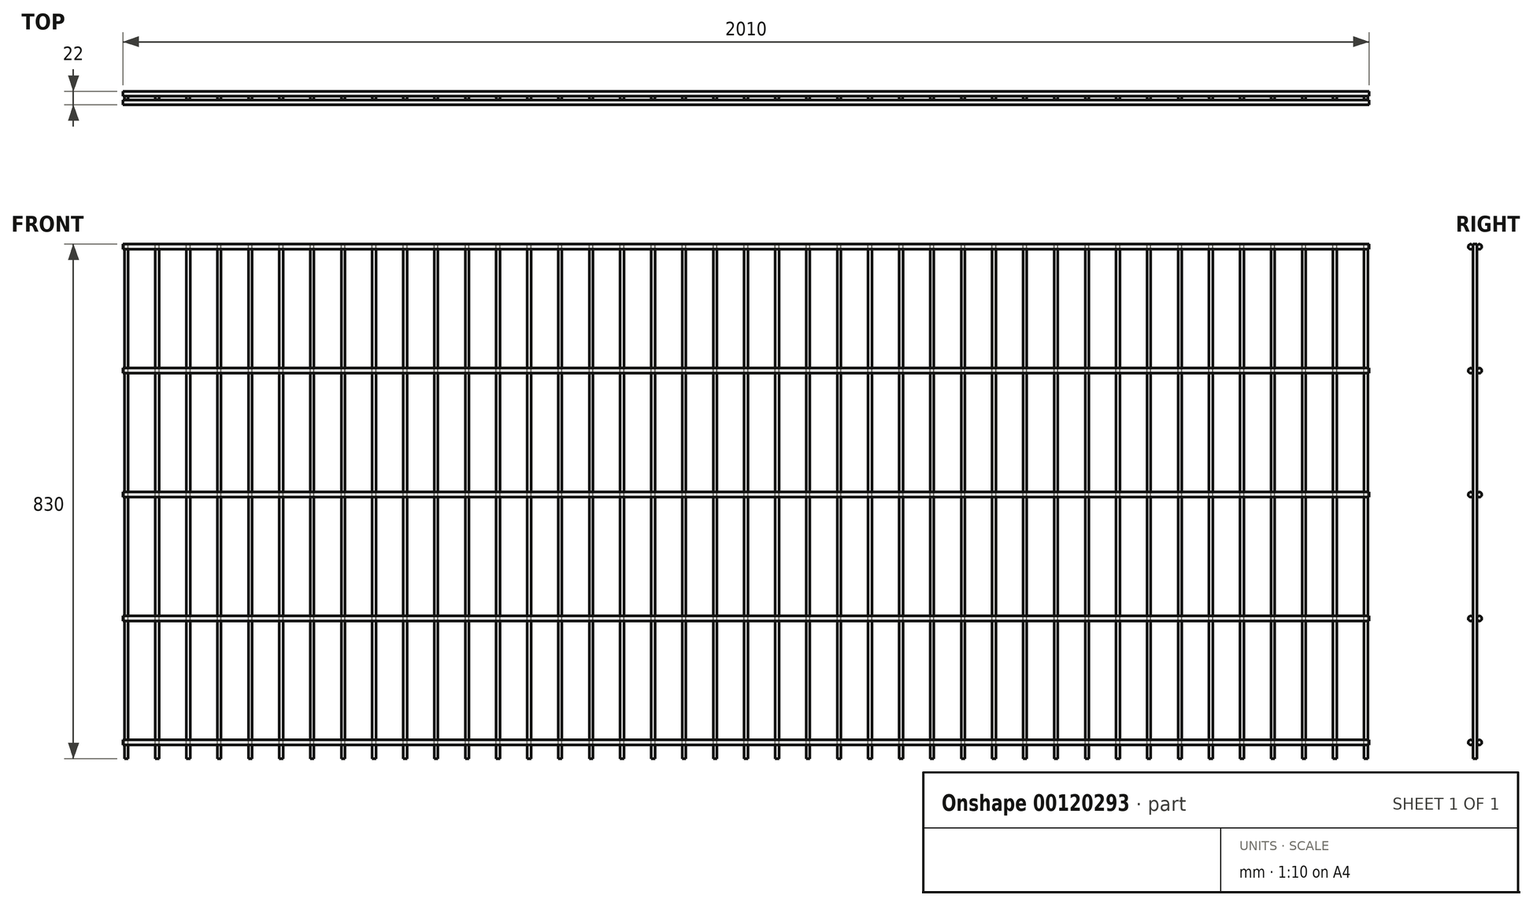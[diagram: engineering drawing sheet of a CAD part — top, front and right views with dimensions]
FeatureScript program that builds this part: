
annotation { "Feature Type Name" : "Feature", "Feature Type Description" : "" }
export const myFeature = defineFeature(function(context is Context, id is Id, definition is map)
    precondition{}
    {
        {
            var Q0;
            Q0=qCreatedBy(makeId("Top.planeOp"),FACE);
            var sketch = newSketch(context, id + "F0", { "sketchPlane" : qUnion([Q0])});
            skCircle(sketch, "E0", {"center": v(-100, 0) * mm, "radius": 3 * mm});
            skCircle(sketch, "E1", {"center": v(-150, 0) * mm, "radius": 3 * mm});
            skCircle(sketch, "E2", {"center": v(-50, 0) * mm, "radius": 3 * mm});
            skCircle(sketch, "E3", {"center": v(0, 0) * mm, "radius": 3 * mm});
            skCircle(sketch, "E4", {"center": v(100, 0) * mm, "radius": 3 * mm});
            skCircle(sketch, "E5", {"center": v(50, 0) * mm, "radius": 3 * mm});
            skCircle(sketch, "E6", {"center": v(150, 0) * mm, "radius": 3 * mm});
            skCircle(sketch, "E7", {"center": v(-450, 0) * mm, "radius": 3 * mm});
            skCircle(sketch, "E8", {"center": v(-500, 0) * mm, "radius": 3 * mm});
            skCircle(sketch, "E9", {"center": v(-400, 0) * mm, "radius": 3 * mm});
            skCircle(sketch, "E10", {"center": v(-350, 0) * mm, "radius": 3 * mm});
            skCircle(sketch, "E11", {"center": v(-250, 0) * mm, "radius": 3 * mm});
            skCircle(sketch, "E12", {"center": v(-300, 0) * mm, "radius": 3 * mm});
            skCircle(sketch, "E13", {"center": v(-200, 0) * mm, "radius": 3 * mm});
            skCircle(sketch, "E14", {"center": v(250, 0) * mm, "radius": 3 * mm});
            skCircle(sketch, "E15", {"center": v(200, 0) * mm, "radius": 3 * mm});
            skCircle(sketch, "E16", {"center": v(300, 0) * mm, "radius": 3 * mm});
            skCircle(sketch, "E17", {"center": v(350, 0) * mm, "radius": 3 * mm});
            skCircle(sketch, "E18", {"center": v(450, 0) * mm, "radius": 3 * mm});
            skCircle(sketch, "E19", {"center": v(400, 0) * mm, "radius": 3 * mm});
            skCircle(sketch, "E20", {"center": v(500, 0) * mm, "radius": 3 * mm});
            skCircle(sketch, "E21", {"center": v(600, 0) * mm, "radius": 3 * mm});
            skCircle(sketch, "E22", {"center": v(550, 0) * mm, "radius": 3 * mm});
            skCircle(sketch, "E23", {"center": v(650, 0) * mm, "radius": 3 * mm});
            skCircle(sketch, "E24", {"center": v(750, 0) * mm, "radius": 3 * mm});
            skCircle(sketch, "E25", {"center": v(700, 0) * mm, "radius": 3 * mm});
            skCircle(sketch, "E26", {"center": v(800, 0) * mm, "radius": 3 * mm});
            skCircle(sketch, "E27", {"center": v(850, 0) * mm, "radius": 3 * mm});
            skCircle(sketch, "E28", {"center": v(950, 0) * mm, "radius": 3 * mm});
            skCircle(sketch, "E29", {"center": v(900, 0) * mm, "radius": 3 * mm});
            skCircle(sketch, "E30", {"center": v(1000, 0) * mm, "radius": 3 * mm});
            skCircle(sketch, "E31", {"center": v(-950, 0) * mm, "radius": 3 * mm});
            skCircle(sketch, "E32", {"center": v(-1000, 0) * mm, "radius": 3 * mm});
            skCircle(sketch, "E33", {"center": v(-900, 0) * mm, "radius": 3 * mm});
            skCircle(sketch, "E34", {"center": v(-800, 0) * mm, "radius": 3 * mm});
            skCircle(sketch, "E35", {"center": v(-850, 0) * mm, "radius": 3 * mm});
            skCircle(sketch, "E36", {"center": v(-750, 0) * mm, "radius": 3 * mm});
            skCircle(sketch, "E37", {"center": v(-700, 0) * mm, "radius": 3 * mm});
            skCircle(sketch, "E38", {"center": v(-600, 0) * mm, "radius": 3 * mm});
            skCircle(sketch, "E39", {"center": v(-650, 0) * mm, "radius": 3 * mm});
            skCircle(sketch, "E40", {"center": v(-550, 0) * mm, "radius": 3 * mm});
            skSolve(sketch);
        }
        {
            var Q0;
            Q0=makeQuery(id+"F0.imprint","IMPRINT",FACE,{"disambiguationData":[TD([[makeQuery(id+"F0.imprint","IMPRINT",EDGE,{"derivedFrom":sQuery(id+"F0.wireOp",EDGE,"E24")}),1.0]])]});
            var Q1;
            Q1=makeQuery(id+"F0.imprint","IMPRINT",FACE,{"disambiguationData":[TD([[makeQuery(id+"F0.imprint","IMPRINT",EDGE,{"derivedFrom":sQuery(id+"F0.wireOp",EDGE,"E40")}),1.0]])]});
            var Q2;
            Q2=makeQuery(id+"F0.imprint","IMPRINT",FACE,{"disambiguationData":[TD([[makeQuery(id+"F0.imprint","IMPRINT",EDGE,{"derivedFrom":sQuery(id+"F0.wireOp",EDGE,"E28")}),1.0]])]});
            var Q3;
            Q3=makeQuery(id+"F0.imprint","IMPRINT",FACE,{"disambiguationData":[TD([[makeQuery(id+"F0.imprint","IMPRINT",EDGE,{"derivedFrom":sQuery(id+"F0.wireOp",EDGE,"E18")}),1.0]])]});
            var Q4;
            Q4=makeQuery(id+"F0.imprint","IMPRINT",FACE,{"disambiguationData":[TD([[makeQuery(id+"F0.imprint","IMPRINT",EDGE,{"derivedFrom":sQuery(id+"F0.wireOp",EDGE,"E34")}),1.0]])]});
            var Q5;
            Q5=makeQuery(id+"F0.imprint","IMPRINT",FACE,{"disambiguationData":[TD([[makeQuery(id+"F0.imprint","IMPRINT",EDGE,{"derivedFrom":sQuery(id+"F0.wireOp",EDGE,"E33")}),1.0]])]});
            var Q6;
            Q6=makeQuery(id+"F0.imprint","IMPRINT",FACE,{"disambiguationData":[TD([[makeQuery(id+"F0.imprint","IMPRINT",EDGE,{"derivedFrom":sQuery(id+"F0.wireOp",EDGE,"E17")}),1.0]])]});
            var Q7;
            Q7=makeQuery(id+"F0.imprint","IMPRINT",FACE,{"disambiguationData":[TD([[makeQuery(id+"F0.imprint","IMPRINT",EDGE,{"derivedFrom":sQuery(id+"F0.wireOp",EDGE,"E37")}),1.0]])]});
            var Q8;
            Q8=makeQuery(id+"F0.imprint","IMPRINT",FACE,{"disambiguationData":[TD([[makeQuery(id+"F0.imprint","IMPRINT",EDGE,{"derivedFrom":sQuery(id+"F0.wireOp",EDGE,"E30")}),1.0]])]});
            var Q9;
            Q9=makeQuery(id+"F0.imprint","IMPRINT",FACE,{"disambiguationData":[TD([[makeQuery(id+"F0.imprint","IMPRINT",EDGE,{"derivedFrom":sQuery(id+"F0.wireOp",EDGE,"E21")}),1.0]])]});
            var Q10;
            Q10=makeQuery(id+"F0.imprint","IMPRINT",FACE,{"disambiguationData":[TD([[makeQuery(id+"F0.imprint","IMPRINT",EDGE,{"derivedFrom":sQuery(id+"F0.wireOp",EDGE,"E25")}),1.0]])]});
            var Q11;
            Q11=makeQuery(id+"F0.imprint","IMPRINT",FACE,{"disambiguationData":[TD([[makeQuery(id+"F0.imprint","IMPRINT",EDGE,{"derivedFrom":sQuery(id+"F0.wireOp",EDGE,"E23")}),1.0]])]});
            var Q12;
            Q12=makeQuery(id+"F0.imprint","IMPRINT",FACE,{"disambiguationData":[TD([[makeQuery(id+"F0.imprint","IMPRINT",EDGE,{"derivedFrom":sQuery(id+"F0.wireOp",EDGE,"E39")}),1.0]])]});
            var Q13;
            Q13=makeQuery(id+"F0.imprint","IMPRINT",FACE,{"disambiguationData":[TD([[makeQuery(id+"F0.imprint","IMPRINT",EDGE,{"derivedFrom":sQuery(id+"F0.wireOp",EDGE,"E27")}),1.0]])]});
            var Q14;
            Q14=makeQuery(id+"F0.imprint","IMPRINT",FACE,{"disambiguationData":[TD([[makeQuery(id+"F0.imprint","IMPRINT",EDGE,{"derivedFrom":sQuery(id+"F0.wireOp",EDGE,"E12")}),1.0]])]});
            var Q15;
            Q15=makeQuery(id+"F0.imprint","IMPRINT",FACE,{"disambiguationData":[TD([[makeQuery(id+"F0.imprint","IMPRINT",EDGE,{"derivedFrom":sQuery(id+"F0.wireOp",EDGE,"E11")}),1.0]])]});
            var Q16;
            Q16=makeQuery(id+"F0.imprint","IMPRINT",FACE,{"disambiguationData":[TD([[makeQuery(id+"F0.imprint","IMPRINT",EDGE,{"derivedFrom":sQuery(id+"F0.wireOp",EDGE,"E10")}),1.0]])]});
            var Q17;
            Q17=makeQuery(id+"F0.imprint","IMPRINT",FACE,{"disambiguationData":[TD([[makeQuery(id+"F0.imprint","IMPRINT",EDGE,{"derivedFrom":sQuery(id+"F0.wireOp",EDGE,"E9")}),1.0]])]});
            var Q18;
            Q18=makeQuery(id+"F0.imprint","IMPRINT",FACE,{"disambiguationData":[TD([[makeQuery(id+"F0.imprint","IMPRINT",EDGE,{"derivedFrom":sQuery(id+"F0.wireOp",EDGE,"E8")}),1.0]])]});
            var Q19;
            Q19=makeQuery(id+"F0.imprint","IMPRINT",FACE,{"disambiguationData":[TD([[makeQuery(id+"F0.imprint","IMPRINT",EDGE,{"derivedFrom":sQuery(id+"F0.wireOp",EDGE,"E31")}),1.0]])]});
            var Q20;
            Q20=makeQuery(id+"F0.imprint","IMPRINT",FACE,{"disambiguationData":[TD([[makeQuery(id+"F0.imprint","IMPRINT",EDGE,{"derivedFrom":sQuery(id+"F0.wireOp",EDGE,"E7")}),1.0]])]});
            var Q21;
            Q21=makeQuery(id+"F0.imprint","IMPRINT",FACE,{"disambiguationData":[TD([[makeQuery(id+"F0.imprint","IMPRINT",EDGE,{"derivedFrom":sQuery(id+"F0.wireOp",EDGE,"E6")}),1.0]])]});
            var Q22;
            Q22=makeQuery(id+"F0.imprint","IMPRINT",FACE,{"disambiguationData":[TD([[makeQuery(id+"F0.imprint","IMPRINT",EDGE,{"derivedFrom":sQuery(id+"F0.wireOp",EDGE,"E5")}),1.0]])]});
            var Q23;
            Q23=makeQuery(id+"F0.imprint","IMPRINT",FACE,{"disambiguationData":[TD([[makeQuery(id+"F0.imprint","IMPRINT",EDGE,{"derivedFrom":sQuery(id+"F0.wireOp",EDGE,"E4")}),1.0]])]});
            var Q24;
            Q24=makeQuery(id+"F0.imprint","IMPRINT",FACE,{"disambiguationData":[TD([[makeQuery(id+"F0.imprint","IMPRINT",EDGE,{"derivedFrom":sQuery(id+"F0.wireOp",EDGE,"E3")}),1.0]])]});
            var Q25;
            Q25=makeQuery(id+"F0.imprint","IMPRINT",FACE,{"disambiguationData":[TD([[makeQuery(id+"F0.imprint","IMPRINT",EDGE,{"derivedFrom":sQuery(id+"F0.wireOp",EDGE,"E2")}),1.0]])]});
            var Q26;
            Q26=makeQuery(id+"F0.imprint","IMPRINT",FACE,{"disambiguationData":[TD([[makeQuery(id+"F0.imprint","IMPRINT",EDGE,{"derivedFrom":sQuery(id+"F0.wireOp",EDGE,"E1")}),1.0]])]});
            var Q27;
            Q27=makeQuery(id+"F0.imprint","IMPRINT",FACE,{"disambiguationData":[TD([[makeQuery(id+"F0.imprint","IMPRINT",EDGE,{"derivedFrom":sQuery(id+"F0.wireOp",EDGE,"E0")}),1.0]])]});
            var Q28;
            Q28=makeQuery(id+"F0.imprint","IMPRINT",FACE,{"disambiguationData":[TD([[makeQuery(id+"F0.imprint","IMPRINT",EDGE,{"derivedFrom":sQuery(id+"F0.wireOp",EDGE,"E32")}),1.0]])]});
            var Q29;
            Q29=makeQuery(id+"F0.imprint","IMPRINT",FACE,{"disambiguationData":[TD([[makeQuery(id+"F0.imprint","IMPRINT",EDGE,{"derivedFrom":sQuery(id+"F0.wireOp",EDGE,"E16")}),1.0]])]});
            var Q30;
            Q30=makeQuery(id+"F0.imprint","IMPRINT",FACE,{"disambiguationData":[TD([[makeQuery(id+"F0.imprint","IMPRINT",EDGE,{"derivedFrom":sQuery(id+"F0.wireOp",EDGE,"E14")}),1.0]])]});
            var Q31;
            Q31=makeQuery(id+"F0.imprint","IMPRINT",FACE,{"disambiguationData":[TD([[makeQuery(id+"F0.imprint","IMPRINT",EDGE,{"derivedFrom":sQuery(id+"F0.wireOp",EDGE,"E13")}),1.0]])]});
            var Q32;
            Q32=makeQuery(id+"F0.imprint","IMPRINT",FACE,{"disambiguationData":[TD([[makeQuery(id+"F0.imprint","IMPRINT",EDGE,{"derivedFrom":sQuery(id+"F0.wireOp",EDGE,"E29")}),1.0]])]});
            var Q33;
            Q33=makeQuery(id+"F0.imprint","IMPRINT",FACE,{"disambiguationData":[TD([[makeQuery(id+"F0.imprint","IMPRINT",EDGE,{"derivedFrom":sQuery(id+"F0.wireOp",EDGE,"E36")}),1.0]])]});
            var Q34;
            Q34=makeQuery(id+"F0.imprint","IMPRINT",FACE,{"disambiguationData":[TD([[makeQuery(id+"F0.imprint","IMPRINT",EDGE,{"derivedFrom":sQuery(id+"F0.wireOp",EDGE,"E15")}),1.0]])]});
            var Q35;
            Q35=makeQuery(id+"F0.imprint","IMPRINT",FACE,{"disambiguationData":[TD([[makeQuery(id+"F0.imprint","IMPRINT",EDGE,{"derivedFrom":sQuery(id+"F0.wireOp",EDGE,"E20")}),1.0]])]});
            var Q36;
            Q36=makeQuery(id+"F0.imprint","IMPRINT",FACE,{"disambiguationData":[TD([[makeQuery(id+"F0.imprint","IMPRINT",EDGE,{"derivedFrom":sQuery(id+"F0.wireOp",EDGE,"E22")}),1.0]])]});
            var Q37;
            Q37=makeQuery(id+"F0.imprint","IMPRINT",FACE,{"disambiguationData":[TD([[makeQuery(id+"F0.imprint","IMPRINT",EDGE,{"derivedFrom":sQuery(id+"F0.wireOp",EDGE,"E38")}),1.0]])]});
            var Q38;
            Q38=makeQuery(id+"F0.imprint","IMPRINT",FACE,{"disambiguationData":[TD([[makeQuery(id+"F0.imprint","IMPRINT",EDGE,{"derivedFrom":sQuery(id+"F0.wireOp",EDGE,"E26")}),1.0]])]});
            var Q39;
            Q39=makeQuery(id+"F0.imprint","IMPRINT",FACE,{"disambiguationData":[TD([[makeQuery(id+"F0.imprint","IMPRINT",EDGE,{"derivedFrom":sQuery(id+"F0.wireOp",EDGE,"E35")}),1.0]])]});
            var Q40;
            Q40=makeQuery(id+"F0.imprint","IMPRINT",FACE,{"disambiguationData":[TD([[makeQuery(id+"F0.imprint","IMPRINT",EDGE,{"derivedFrom":sQuery(id+"F0.wireOp",EDGE,"E19")}),1.0]])]});
            extrude(context, id + "F1", {"entities" : qUnion([Q0, Q1, Q2, Q3, Q4, Q5, Q6, Q7, Q8, Q9, Q10, Q11, Q12, Q13, Q14, Q15, Q16, Q17, Q18, Q19, Q20, Q21, Q22, Q23, Q24, Q25, Q26, Q27, Q28, Q29, Q30, Q31, Q32, Q33, Q34, Q35, Q36, Q37, Q38, Q39, Q40]), "oppositeDirection" : true, "depth" : 830 * mm});
        }
        {
            var Q0;
            Q0=qCreatedBy(makeId("Right.planeOp"),FACE);
            var sketch = newSketch(context, id + "F2", { "sketchPlane" : qUnion([Q0])});
            skLineSegment(sketch, "E41", {"start": v(-7, 0) * mm, "end": v(-7, -830.13) * mm, "construction": true});
            skLineSegment(sketch, "E42", {"start": v(7, 0) * mm, "end": v(7, -829.8) * mm, "construction": true});
            skCircle(sketch, "E43", {"center": v(7, -4) * mm, "radius": 4 * mm});
            skCircle(sketch, "E44", {"center": v(-7, -4) * mm, "radius": 4 * mm});
            skCircle(sketch, "E45", {"center": v(7, -204) * mm, "radius": 4 * mm});
            skCircle(sketch, "E46", {"center": v(-7, -204) * mm, "radius": 4 * mm});
            skCircle(sketch, "E47", {"center": v(7, -404) * mm, "radius": 4 * mm});
            skCircle(sketch, "E48", {"center": v(-7, -404) * mm, "radius": 4 * mm});
            skCircle(sketch, "E49", {"center": v(7, -604) * mm, "radius": 4 * mm});
            skCircle(sketch, "E50", {"center": v(-7, -604) * mm, "radius": 4 * mm});
            skCircle(sketch, "E51", {"center": v(7, -804) * mm, "radius": 4 * mm});
            skCircle(sketch, "E52", {"center": v(-7, -804) * mm, "radius": 4 * mm});
            skSolve(sketch);
        }
        {
            var Q0;
            Q0 = qSketchRegion(id + "F2", true);
            extrude(context, id + "F3", {"entities" : qUnion([Q0]), "depth" : 2010 * mm, "symmetric" : true});
        }
    });
